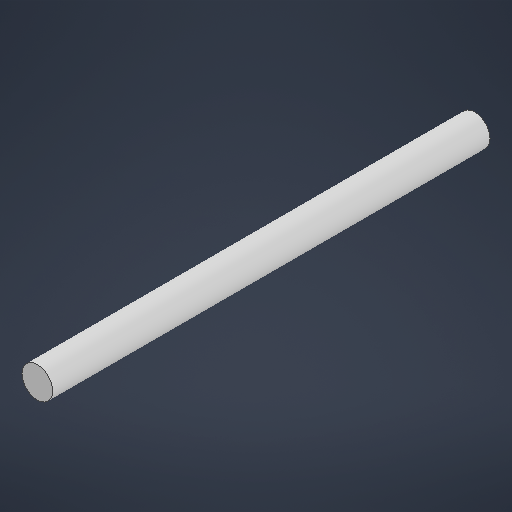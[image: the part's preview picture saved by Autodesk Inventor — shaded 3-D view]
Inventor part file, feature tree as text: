
AUTODESK INVENTOR PART (.ipt)
format: ipt  version: 2025.3 (Build 293356030, 356C)  size: 180,224 bytes
history: native  units: mm
features: extrude x1, sketch x1
ambient origin geometry x8: Origin, YZ Plane, XZ Plane, XY Plane, X Axis, Y Axis, Z Axis, Center Point
bodies: Solid1 (feature_tree)
feature tree (2):
  extrude  "Extrusion1"  Depth=100.0mm TaperAngle=0.0deg
  sketch  "Sketch1"  dims[d0=7.0mm d1=100.0mm d2=0.0mm]
